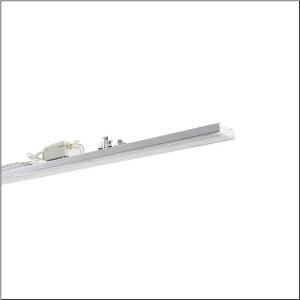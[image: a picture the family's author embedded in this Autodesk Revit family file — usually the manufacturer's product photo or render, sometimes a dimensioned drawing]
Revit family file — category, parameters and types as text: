
# Revit family: licross_r__21_recessed_ho_52tl11mn4fxs_9277
name_source: partatom
category: Lighting Fixtures
units: mm (PartAtom-declared; Revit-internal decimal feet)

## family parameters
Cut with Voids When Loaded = No
Host = Face
Light Source = No
Part Type = Normal
Room Calculation Point = No
Round Connector Dimension = Use Diameter
Shared = No

## types (1)
- --- (1 x LED, 15070 lm, 83.1 W, 4000K)
    Apparent Load = 83 VA
    CIE Flux Codes = 87 95 99 100 100
    Color Rendering = 80
    Color Temperature = 4000K
    Default Elevation = 1800 mm
    Description = Licross® 21 Recessed HO, luminaire insert, of sheet steel, galvanised, coil coated, white, length: 1.500mm, width: 66mm, height: 67mm, LED rated luminous flux: 15.060lm, light colour: 840, control gear: ON/OFF Multilumen, with plug, 3-pole, with phase selection, mains connection: 220..240V, AC, 50/60Hz, rated input power: 83W, halogen-free wiring, primary light control with lens, of plastic, primary optical cover: cover, of PMMA, light emission: direct distribution, primary light characteristic: symmetric, protection rating (complete): IP40, insulation class (complete): insulation class I (protective earthing), certification: CE, ENEC, VDE, UKCA, protection symbol: D if used in an environment without relevant dust loads with corresponding accessories, impact resistance: IK06, permissible ambient temperature for indoor applications: -35..+30°C, corresponds to IFS (International Featured Standards) requirements for safety and quality in the food industry, reducing of maximum allowable ambient temperature of 5°C with ceiling mounting, LABS conformity tested according to VDMA 24364:2018-05, packaging unit: 1 piece
    Height = 58 mm
    Lamp = 1 x LED
    Lamp Light Flux = 15070 lm
    Lamp Power = 83.1 W
    Lamp count = 1
    Length = 1500 mm
    Luminous efficacy = 181 lm/W
    Manufacturer = Siteco
    ModVariant = No
    Model = 52TL11MN4FXS
    Mounting Place = Ceiling
    Mounting Type = Pendant
    Number of Poles = 1
    OnlyDefault = Yes
    Power Factor = 1
    Product Name = Licross® 21 Recessed HO
    Product group = luminaire insert
    ProductGroupID = 901
    Protection Class = Protection class I
    Protection Degree = IP 40
    RLX_Detail_Level = 1
    RLX_Emergency_Light_Flux = 0 lm
    RLX_Emergency_Type = 0
    RLX_Emergency_Type_DB = No
    RlxData = <blob elided: 22197 chars, md5=bb91b82d>
    Socket = socket
    Standby Power = 0 W
    System Light Flux = 15070 lm
    System Power = 83 W
    Type Comments = factory setting: luminous flux: 100 % | (A | C | E) | 195 mA
    Type Image = l_1296930.jpg
    URL = http://relux.com
    VarID = @adj_038193
    Voltage = 0 V
    Weight = 0.00 kg
    Width = 66 mm

## geometry (parser evidence)
native form markers: Blend x4, Sweep x11
no freeform markers — native parametric forms only
